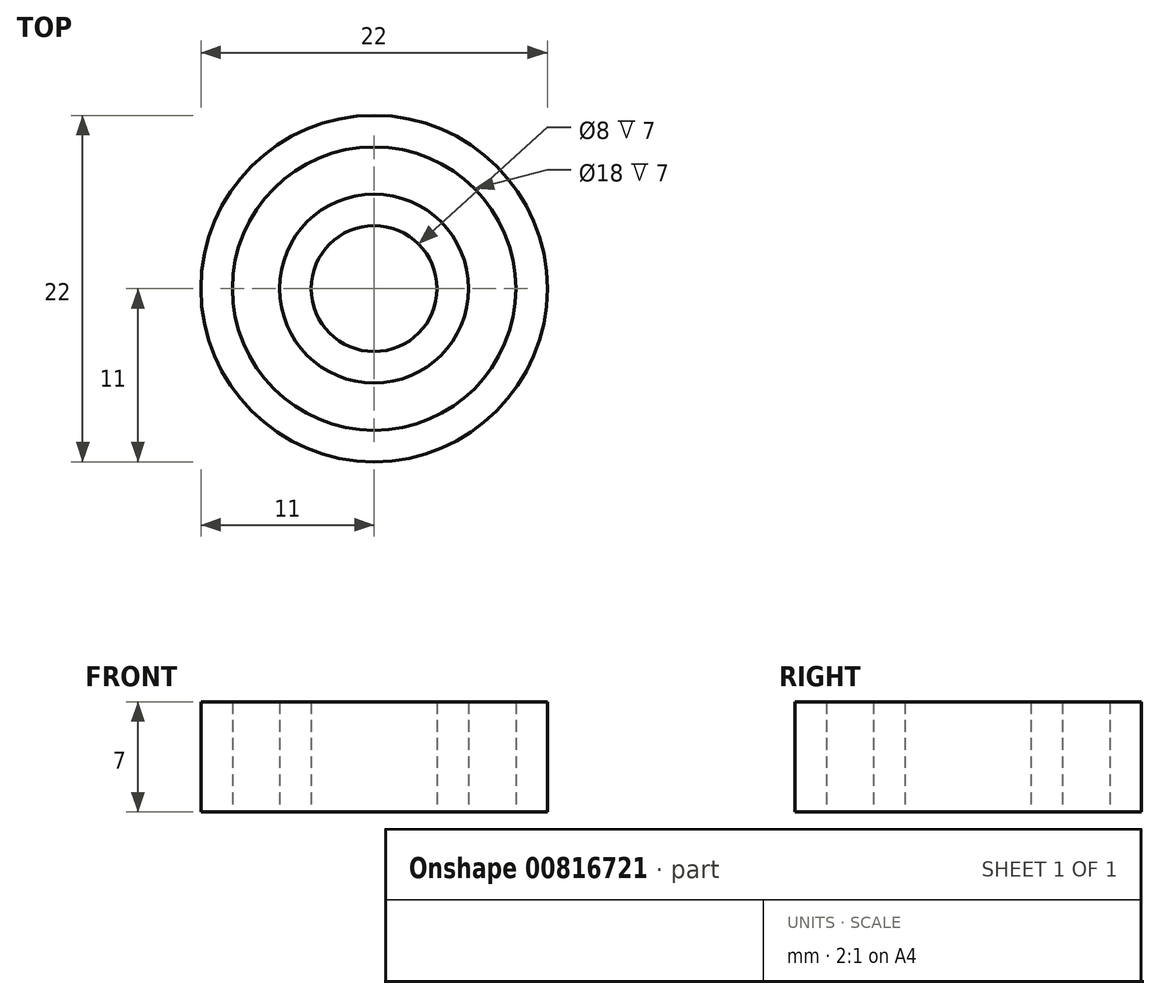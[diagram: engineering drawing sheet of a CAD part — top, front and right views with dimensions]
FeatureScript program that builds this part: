
annotation { "Feature Type Name" : "Feature", "Feature Type Description" : "" }
export const myFeature = defineFeature(function(context is Context, id is Id, definition is map)
    precondition{}
    {
        {
            var Q0;
            Q0=qCreatedBy(makeId("Top.planeOp"),FACE);
            var sketch = newSketch(context, id + "F0", { "sketchPlane" : qUnion([Q0])});
            skCircle(sketch, "E0", {"center": v(0, 0) * mm, "radius": 6 * mm});
            skCircle(sketch, "E1", {"center": v(0, 0) * mm, "radius": 4 * mm});
            skCircle(sketch, "E2", {"center": v(0, 0) * mm, "radius": 11 * mm});
            skCircle(sketch, "E3", {"center": v(0, 0) * mm, "radius": 9 * mm});
            skSolve(sketch);
        }
        {
            var Q0;
            Q0=makeQuery(id+"F0.imprint","IMPRINT",FACE,{"disambiguationData":[TD([[makeQuery(id+"F0.imprint","IMPRINT",EDGE,{"derivedFrom":sQuery(id+"F0.wireOp",EDGE,"E2")}),1.0]])]});
            var Q1;
            Q1=makeQuery(id+"F0.imprint","IMPRINT",FACE,{"disambiguationData":[TD([[makeQuery(id+"F0.imprint","IMPRINT",EDGE,{"derivedFrom":sQuery(id+"F0.wireOp",EDGE,"E0")}),1.0]])]});
            extrude(context, id + "F1", {"entities" : qUnion([Q0, Q1]), "depth" : 7 * mm, "offsetDistance" : 25 * mm});
        }
    });
